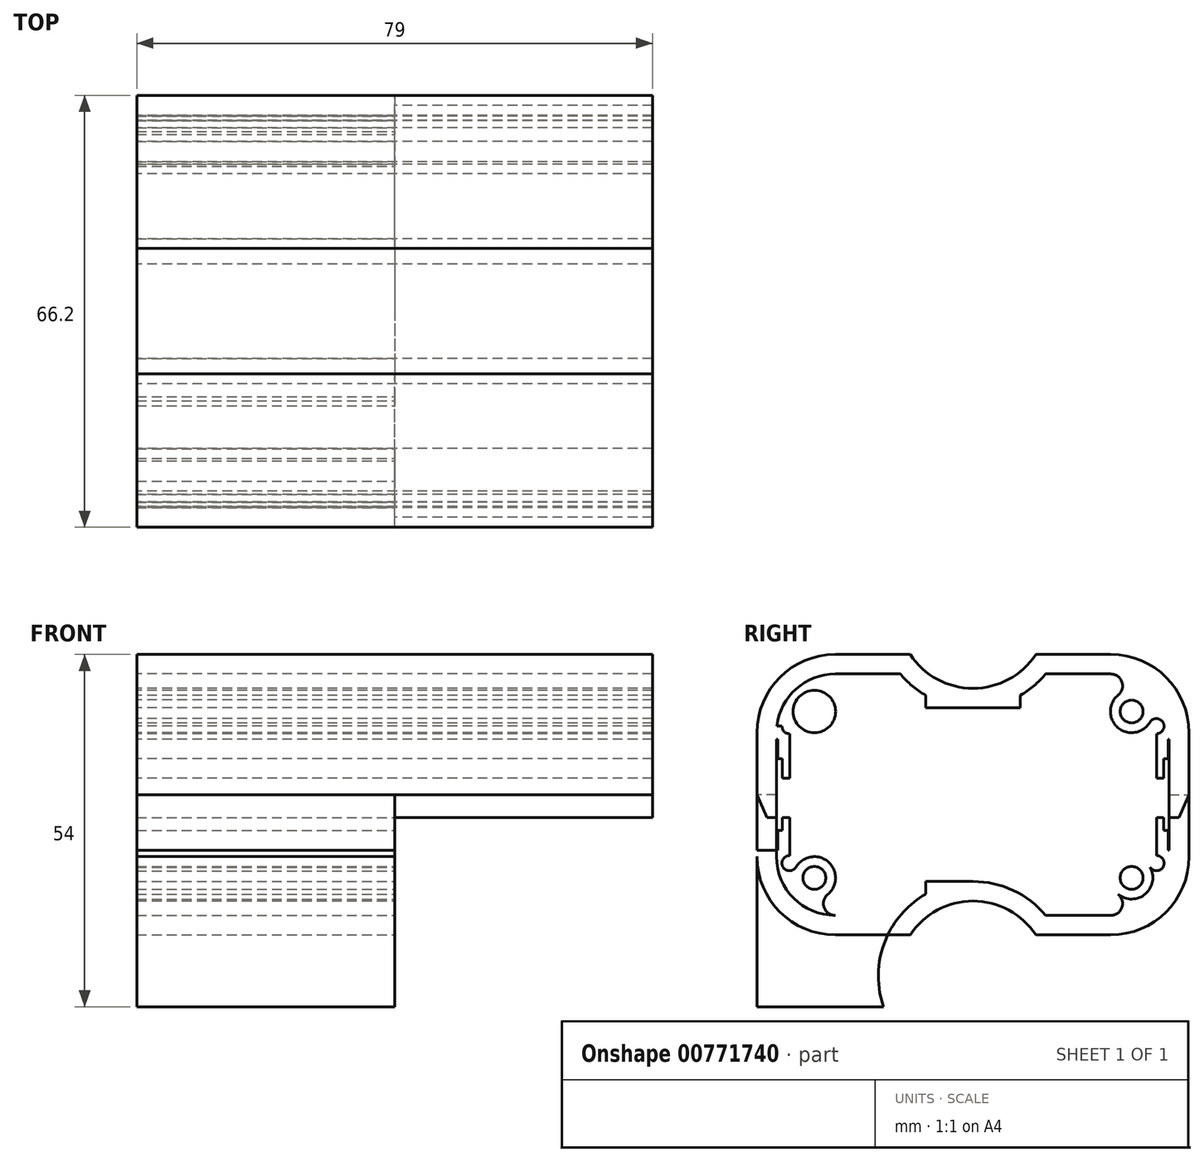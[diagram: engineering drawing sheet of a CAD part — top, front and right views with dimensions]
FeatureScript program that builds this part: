
annotation { "Feature Type Name" : "Feature", "Feature Type Description" : "" }
export const myFeature = defineFeature(function(context is Context, id is Id, definition is map)
    precondition{}
    {
        {
            var Q0;
            Q0=qCreatedBy(makeId("Right.planeOp"),FACE);
            var sketch = newSketch(context, id + "F0", { "sketchPlane" : qUnion([Q0])});
            skLineSegment(sketch, "E0.bottom", {"start": v(-33.1, -16.8) * mm, "end": v(-33.1, -3.8) * mm});
            skLineSegment(sketch, "E0.top", {"start": v(33.1, -16.8) * mm, "end": v(33.1, 19.2) * mm});
            skLineSegment(sketch, "E0.left", {"start": v(-33.1, -16.8) * mm, "end": v(33.1, -16.8) * mm});
            skLineSegment(sketch, "E0.right", {"start": v(-33.1, 19.2) * mm, "end": v(33.1, 19.2) * mm});
            skPoint(sketch, "E0.middle", {"position": v(0, 1.2) * mm});
            skLineSegment(sketch, "E1.bottom", {"start": v(-33.1, -16.8) * mm, "end": v(-33.1, 19.2) * mm});
            skLineSegment(sketch, "E1.right", {"start": v(-21.1, 8.2) * mm, "end": v(21.1, 8.2) * mm});
            skPoint(sketch, "E2.visualSharp", {"position": v(33.1, 8.2) * mm});
            skArc(sketch, "E2.filletArc", {"start": v(33.1, -3.8) * mm, "mid": v(29.59, 4.69) * mm, "end": v(21.1, 8.2) * mm});
            skPoint(sketch, "E3.newPointB", {"position": v(-33.1, 19.2) * mm});
            skArc(sketch, "E3.filletArc", {"start": v(-21.1, 8.2) * mm, "mid": v(-29.59, 4.69) * mm, "end": v(-33.1, -3.8) * mm});
            skLineSegment(sketch, "E4.0", {"start": v(-30.1, -16.8) * mm, "end": v(-30.1, -3.8) * mm});
            skLineSegment(sketch, "E4.1", {"start": v(30.04, -16.8) * mm, "end": v(30.04, -2.8) * mm});
            skArc(sketch, "E4.2", {"start": v(30.04, -2.8) * mm, "mid": v(27.1, 2.9) * mm, "end": v(21.1, 5.2) * mm});
            skLineSegment(sketch, "E4.3", {"start": v(-21.1, 5.2) * mm, "end": v(21.1, 5.2) * mm});
            skArc(sketch, "E4.4", {"start": v(-21.1, 5.2) * mm, "mid": v(-27.46, 2.56) * mm, "end": v(-30.1, -3.8) * mm});
            skCircle(sketch, "E5", {"center": v(0, 14.5) * mm, "radius": 11.5 * mm});
            skCircle(sketch, "E6.0", {"center": v(0, 14.5) * mm, "radius": 14.5 * mm});
            skLineSegment(sketch, "E7", {"start": v(0, 3) * mm, "end": v(0, 0) * mm, "construction": true});
            skLineSegment(sketch, "E8.left", {"start": v(7.25, 0) * mm, "end": v(-7.25, 0) * mm});
            skPoint(sketch, "E8.middle", {"position": v(0, 1.5) * mm});
            skCircle(sketch, "E9", {"center": v(24.3, -0.55) * mm, "radius": 1.75 * mm});
            skCircle(sketch, "E10.0", {"center": v(24.3, -0.55) * mm, "radius": 3.25 * mm});
            skLineSegment(sketch, "E11.top", {"start": v(28.1, -10.8) * mm, "end": v(28.1, -2.8) * mm});
            skLineSegment(sketch, "E11.right", {"start": v(33.1, -2.8) * mm, "end": v(28.1, -2.8) * mm});
            skLineSegment(sketch, "E12.bottom", {"start": v(28.1, -2.8) * mm, "end": v(28.1, -10.8) * mm});
            skLineSegment(sketch, "E13.left", {"start": v(28.1, -2.8) * mm, "end": v(30.04, -2.8) * mm});
            skLineSegment(sketch, "E13.right", {"start": v(29.9, -4.8) * mm, "end": v(33.1, -4.8) * mm});
            skLineSegment(sketch, "E14.top", {"start": v(29.9, -4.8) * mm, "end": v(29.9, -7.8) * mm});
            skLineSegment(sketch, "E14.left", {"start": v(30.04, -2.8) * mm, "end": v(33.1, -2.8) * mm});
            skLineSegment(sketch, "E14.right", {"start": v(29.2, -7.8) * mm, "end": v(29.9, -7.8) * mm});
            skLineSegment(sketch, "E15.top", {"start": v(29.2, -7.8) * mm, "end": v(29.2, -10.8) * mm});
            skLineSegment(sketch, "E15.right", {"start": v(28.1, -10.8) * mm, "end": v(29.2, -10.8) * mm});
            skCircle(sketch, "E16", {"center": v(21.1, 3.38) * mm, "radius": 1.82 * mm});
            skPoint(sketch, "E16.second.point", {"position": v(21.1, 5.2) * mm});
            skPoint(sketch, "E16.third.point", {"position": v(21.1, 5.2) * mm});
            skCircle(sketch, "E17", {"center": v(28.1, -2.8) * mm, "radius": 1.17 * mm});
            skLineSegment(sketch, "E18", {"start": v(28.1, -2.8) * mm, "end": v(28.92, -3.62) * mm, "construction": true});
            skLineSegment(sketch, "E19.bottom", {"start": v(33.1, -2.8) * mm, "end": v(33.1, -9.6) * mm});
            skLineSegment(sketch, "E19.top", {"start": v(30.04, -2.8) * mm, "end": v(30.04, -9.6) * mm});
            skLineSegment(sketch, "E19.left", {"start": v(33.1, -2.8) * mm, "end": v(30.04, -2.8) * mm});
            skLineSegment(sketch, "E19.right", {"start": v(33.1, -9.6) * mm, "end": v(30.04, -9.6) * mm});
            skLineSegment(sketch, "E20", {"start": v(33.1, -13.3) * mm, "end": v(31.57, -16.8) * mm});
            skLineSegment(sketch, "E21", {"start": v(33.1, -16.8) * mm, "end": v(30.04, -16.8) * mm, "construction": true});
            skLineSegment(sketch, "E22", {"start": v(0, -16.8) * mm, "end": v(0, 29) * mm, "construction": true});
            skCircle(sketch, "E23.MirrorC", {"center": v(-21.1, 3.38) * mm, "radius": 1.82 * mm});
            skCircle(sketch, "E24.MirrorC", {"center": v(-24.3, -0.55) * mm, "radius": 3.25 * mm});
            skCircle(sketch, "E25.MirrorC", {"center": v(-24.3, -0.55) * mm, "radius": 1.75 * mm});
            skCircle(sketch, "E26.MirrorC", {"center": v(-28.1, -2.8) * mm, "radius": 1.17 * mm});
            skLineSegment(sketch, "E27.MirrorCS", {"start": v(-28.1, -2.8) * mm, "end": v(-30.04, -2.8) * mm});
            skLineSegment(sketch, "E28.MirrorCS", {"start": v(-28.1, -2.8) * mm, "end": v(-28.1, -10.8) * mm});
            skLineSegment(sketch, "E29.MirrorCS", {"start": v(-28.1, -10.8) * mm, "end": v(-29.2, -10.8) * mm});
            skLineSegment(sketch, "E30.MirrorCS", {"start": v(-29.2, -7.8) * mm, "end": v(-29.2, -10.8) * mm});
            skLineSegment(sketch, "E31.MirrorCS", {"start": v(-29.2, -7.8) * mm, "end": v(-29.9, -7.8) * mm});
            skLineSegment(sketch, "E32.MirrorCS", {"start": v(-29.9, -4.8) * mm, "end": v(-29.9, -7.8) * mm});
            skLineSegment(sketch, "E33.MirrorCS", {"start": v(-29.9, -4.8) * mm, "end": v(-33.1, -4.8) * mm});
            skLineSegment(sketch, "E34.MirrorCS", {"start": v(-33.1, -13.3) * mm, "end": v(-31.57, -16.8) * mm});
            skLineSegment(sketch, "E35.bottom", {"start": v(33.1, -16.8) * mm, "end": v(33.1, 5.2) * mm, "construction": true});
            skLineSegment(sketch, "E35.top", {"start": v(21.1, -16.8) * mm, "end": v(21.1, 5.2) * mm, "construction": true});
            skLineSegment(sketch, "E35.left", {"start": v(33.1, -16.8) * mm, "end": v(21.1, -16.8) * mm, "construction": true});
            skLineSegment(sketch, "E35.right", {"start": v(33.1, 5.2) * mm, "end": v(21.1, 5.2) * mm, "construction": true});
            skLineSegment(sketch, "E36", {"start": v(7.25, 0) * mm, "end": v(7.25, 1.94) * mm});
            skLineSegment(sketch, "E37", {"start": v(7.25, 1.94) * mm, "end": v(-7.25, 1.94) * mm});
            skLineSegment(sketch, "E38", {"start": v(-7.25, 1.94) * mm, "end": v(-7.25, 0) * mm});
            skLineSegment(sketch, "E39", {"start": v(21.1, 5.2) * mm, "end": v(24.3, -0.55) * mm, "construction": true});
            skLineSegment(sketch, "E40", {"start": v(33.1, -13.3) * mm, "end": v(30.04, -13.3) * mm});
            skLineSegment(sketch, "E41", {"start": v(-33.1, -13.3) * mm, "end": v(-30.1, -13.3) * mm});
            skLineSegment(sketch, "E42", {"start": v(-53, -13.3) * mm, "end": v(50.01, -13.3) * mm, "construction": true});
            skLineSegment(sketch, "E43.MirrorCS", {"start": v(28.1, -23.8) * mm, "end": v(30.04, -23.8) * mm});
            skLineSegment(sketch, "E44.MirrorCS", {"start": v(28.1, -23.8) * mm, "end": v(28.92, -22.98) * mm, "construction": true});
            skCircle(sketch, "E45.MirrorC", {"center": v(28.1, -23.8) * mm, "radius": 1.17 * mm});
            skLineSegment(sketch, "E46.MirrorCS", {"start": v(33.1, -23.8) * mm, "end": v(30.04, -23.8) * mm});
            skLineSegment(sketch, "E47.MirrorCS", {"start": v(30.04, -23.8) * mm, "end": v(33.1, -23.8) * mm});
            skLineSegment(sketch, "E48.MirrorCS", {"start": v(28.1, -15.8) * mm, "end": v(29.2, -15.8) * mm});
            skLineSegment(sketch, "E49.MirrorCS", {"start": v(33.1, -23.8) * mm, "end": v(28.1, -23.8) * mm});
            skLineSegment(sketch, "E50.MirrorCS", {"start": v(28.1, -23.8) * mm, "end": v(28.1, -15.8) * mm});
            skCircle(sketch, "E51.MirrorC", {"center": v(-28.1, -23.8) * mm, "radius": 1.17 * mm});
            skLineSegment(sketch, "E52.MirrorCS", {"start": v(29.9, -21.8) * mm, "end": v(29.9, -18.8) * mm});
            skLineSegment(sketch, "E53.MirrorCS", {"start": v(29.2, -18.8) * mm, "end": v(29.2, -15.8) * mm});
            skLineSegment(sketch, "E54.MirrorCS", {"start": v(33.1, -17) * mm, "end": v(30.04, -17) * mm});
            skLineSegment(sketch, "E55.MirrorCS", {"start": v(30.04, -23.8) * mm, "end": v(30.04, -17) * mm});
            skLineSegment(sketch, "E56.MirrorCS", {"start": v(-28.1, -23.8) * mm, "end": v(-30.04, -23.8) * mm});
            skLineSegment(sketch, "E57.MirrorCS", {"start": v(33.1, -13.3) * mm, "end": v(31.57, -9.8) * mm});
            skLineSegment(sketch, "E58.MirrorCS", {"start": v(29.2, -18.8) * mm, "end": v(29.9, -18.8) * mm});
            skLineSegment(sketch, "E59.MirrorCS", {"start": v(7.25, -26.6) * mm, "end": v(7.25, -28.54) * mm});
            skLineSegment(sketch, "E60.MirrorCS", {"start": v(-29.2, -18.8) * mm, "end": v(-29.9, -18.8) * mm});
            skLineSegment(sketch, "E61.MirrorCS", {"start": v(-7.25, -28.54) * mm, "end": v(-7.25, -26.6) * mm});
            skLineSegment(sketch, "E62.MirrorCS", {"start": v(30.04, -9.8) * mm, "end": v(30.04, -23.8) * mm});
            skCircle(sketch, "E63.MirrorC", {"center": v(-24.3, -26.05) * mm, "radius": 1.75 * mm});
            skLineSegment(sketch, "E64.MirrorCS", {"start": v(29.9, -21.8) * mm, "end": v(33.1, -21.8) * mm});
            skLineSegment(sketch, "E65.MirrorCS", {"start": v(28.1, -15.8) * mm, "end": v(28.1, -23.8) * mm});
            skLineSegment(sketch, "E66.MirrorCS", {"start": v(-28.1, -15.8) * mm, "end": v(-29.2, -15.8) * mm});
            skLineSegment(sketch, "E67.MirrorCS", {"start": v(-29.9, -21.8) * mm, "end": v(-33.1, -21.8) * mm});
            skLineSegment(sketch, "E68.MirrorCS", {"start": v(-33.1, -13.3) * mm, "end": v(-31.57, -9.8) * mm});
            skLineSegment(sketch, "E69.MirrorCS", {"start": v(-29.9, -21.8) * mm, "end": v(-29.9, -18.8) * mm});
            skLineSegment(sketch, "E70.MirrorCS", {"start": v(-29.2, -18.8) * mm, "end": v(-29.2, -15.8) * mm});
            skLineSegment(sketch, "E71.MirrorCS", {"start": v(33.1, -9.8) * mm, "end": v(30.04, -9.8) * mm, "construction": true});
            skLineSegment(sketch, "E72.MirrorCS", {"start": v(33.1, -23.8) * mm, "end": v(33.1, -17) * mm});
            skLineSegment(sketch, "E73.MirrorCS", {"start": v(-30.1, -9.8) * mm, "end": v(-30.1, -22.8) * mm});
            skLineSegment(sketch, "E74.MirrorCS", {"start": v(-33.1, -9.8) * mm, "end": v(-33.1, -22.8) * mm});
            skLineSegment(sketch, "E75.MirrorCS", {"start": v(0, -29.6) * mm, "end": v(0, -26.6) * mm, "construction": true});
            skPoint(sketch, "E76.MirrorP", {"position": v(21.1, -31.8) * mm});
            skCircle(sketch, "E77.MirrorC", {"center": v(21.1, -29.98) * mm, "radius": 1.82 * mm});
            skCircle(sketch, "E78.MirrorC", {"center": v(-21.1, -29.98) * mm, "radius": 1.82 * mm});
            skLineSegment(sketch, "E79.MirrorCS", {"start": v(-28.1, -23.8) * mm, "end": v(-28.1, -15.8) * mm});
            skPoint(sketch, "E80.MirrorP", {"position": v(0, -28.1) * mm});
            skLineSegment(sketch, "E81.MirrorCS", {"start": v(33.1, -31.8) * mm, "end": v(21.1, -31.8) * mm, "construction": true});
            skLineSegment(sketch, "E82.MirrorCS", {"start": v(7.25, -28.54) * mm, "end": v(-7.25, -28.54) * mm});
            skPoint(sketch, "E83.MirrorP", {"position": v(33.1, -34.8) * mm});
            skLineSegment(sketch, "E84.MirrorCS", {"start": v(-33.1, -9.8) * mm, "end": v(33.1, -9.8) * mm});
            skArc(sketch, "E85.MirrorCS", {"start": v(-21.1, -34.8) * mm, "mid": v(-29.59, -31.29) * mm, "end": v(-33.1, -22.8) * mm});
            skLineSegment(sketch, "E86.MirrorCS", {"start": v(-21.1, -31.8) * mm, "end": v(21.1, -31.8) * mm});
            skArc(sketch, "E87.MirrorCS", {"start": v(30.04, -23.8) * mm, "mid": v(27.1, -29.5) * mm, "end": v(21.1, -31.8) * mm});
            skLineSegment(sketch, "E88.MirrorCS", {"start": v(-21.1, -34.8) * mm, "end": v(21.1, -34.8) * mm});
            skCircle(sketch, "E89.MirrorC", {"center": v(0, -41.1) * mm, "radius": 11.5 * mm});
            skLineSegment(sketch, "E90.MirrorCS", {"start": v(7.25, -26.6) * mm, "end": v(-7.25, -26.6) * mm});
            skCircle(sketch, "E91.MirrorC", {"center": v(24.3, -26.05) * mm, "radius": 1.75 * mm});
            skArc(sketch, "E92.MirrorCS", {"start": v(-21.1, -31.8) * mm, "mid": v(-27.46, -29.16) * mm, "end": v(-30.1, -22.8) * mm});
            skLineSegment(sketch, "E93.MirrorCS", {"start": v(0, -9.8) * mm, "end": v(0, -55.6) * mm, "construction": true});
            skPoint(sketch, "E94.MirrorP", {"position": v(0, -27.8) * mm});
            skCircle(sketch, "E95.MirrorC", {"center": v(-24.3, -26.05) * mm, "radius": 3.25 * mm});
            skCircle(sketch, "E96.MirrorC", {"center": v(24.3, -26.05) * mm, "radius": 3.25 * mm});
            skLineSegment(sketch, "E97.MirrorCS", {"start": v(-33.1, -45.8) * mm, "end": v(33.1, -45.8) * mm});
            skLineSegment(sketch, "E98.MirrorCS", {"start": v(33.1, -9.8) * mm, "end": v(21.1, -9.8) * mm, "construction": true});
            skLineSegment(sketch, "E99.MirrorCS", {"start": v(21.1, -9.8) * mm, "end": v(21.1, -31.8) * mm, "construction": true});
            skLineSegment(sketch, "E100.MirrorCS", {"start": v(-33.1, -9.8) * mm, "end": v(-33.1, -45.8) * mm});
            skCircle(sketch, "E101.MirrorC", {"center": v(0, -41.1) * mm, "radius": 14.5 * mm});
            skPoint(sketch, "E102.MirrorP", {"position": v(-33.1, -45.8) * mm});
            skLineSegment(sketch, "E103.MirrorCS", {"start": v(33.1, -9.8) * mm, "end": v(33.1, -45.8) * mm});
            skLineSegment(sketch, "E104.MirrorCS", {"start": v(33.1, -9.8) * mm, "end": v(33.1, -31.8) * mm, "construction": true});
            skLineSegment(sketch, "E105.MirrorCS", {"start": v(21.1, -31.8) * mm, "end": v(24.3, -26.05) * mm, "construction": true});
            skArc(sketch, "E106.MirrorCS", {"start": v(33.1, -22.8) * mm, "mid": v(29.59, -31.29) * mm, "end": v(21.1, -34.8) * mm});
            skSolve(sketch);
        }
        {
            var Q0;
            {var subQ0=sQuery(id+"F0.wireOp",EDGE,"E6.0");var subQ1=sQuery(id+"F0.wireOp",EDGE,"E1.right");var subQ2=makeQuery(id+"F0.imprint","INTERSECT",VERTEX,{"disambiguationData":[OD(0.0)],"derivedFrom":[subQ1,subQ0]});Q0=makeQuery(id+"F0.imprint","IMPRINT",FACE,{"disambiguationData":[TD([[makeQuery(id+"F0.imprint","IMPRINT",EDGE,{"disambiguationData":[TD([[subQ2,-1.0]])],"derivedFrom":subQ1}),-1.0]])]});}
            var Q1;
            {var subQ0=sQuery(id+"F0.wireOp",EDGE,"E37");Q1=makeQuery(id+"F0.imprint","IMPRINT",FACE,{"disambiguationData":[TD([[makeQuery(id+"F0.imprint","IMPRINT",EDGE,{"derivedFrom":subQ0}),-1.0]])]});}
            var Q2;
            {var subQ0=sQuery(id+"F0.wireOp",EDGE,"E38");Q2=makeQuery(id+"F0.imprint","IMPRINT",FACE,{"disambiguationData":[TD([[makeQuery(id+"F0.imprint","IMPRINT",EDGE,{"derivedFrom":subQ0}),1.0]])]});}
            var Q3;
            {var subQ0=sQuery(id+"F0.wireOp",EDGE,"E37");Q3=makeQuery(id+"F0.imprint","IMPRINT",FACE,{"disambiguationData":[TD([[makeQuery(id+"F0.imprint","IMPRINT",EDGE,{"derivedFrom":subQ0}),1.0]])]});}
            var Q4;
            {var subQ0=sQuery(id+"F0.wireOp",EDGE,"E36");Q4=makeQuery(id+"F0.imprint","IMPRINT",FACE,{"disambiguationData":[TD([[makeQuery(id+"F0.imprint","IMPRINT",EDGE,{"derivedFrom":subQ0}),1.0]])]});}
            var Q5;
            {var subQ0=sQuery(id+"F0.wireOp",EDGE,"E5");var subQ1=sQuery(id+"F0.wireOp",EDGE,"E1.right");var subQ2=makeQuery(id+"F0.imprint","INTERSECT",VERTEX,{"disambiguationData":[OD(1.0)],"derivedFrom":[subQ1,subQ0]});Q5=makeQuery(id+"F0.imprint","IMPRINT",FACE,{"disambiguationData":[TD([[makeQuery(id+"F0.imprint","IMPRINT",EDGE,{"disambiguationData":[TD([[subQ2,-1.0]])],"derivedFrom":subQ1}),-1.0]])]});}
            var Q6;
            {var subQ1=sQuery(id+"F0.wireOp",EDGE,"E4.2");Q6=makeQuery(id+"F0.imprint","IMPRINT",FACE,{"disambiguationData":[TD([[makeQuery(id+"F0.imprint","IMPRINT",EDGE,{"derivedFrom":subQ1}),-1.0]])]});}
            var Q7;
            {var subQ1=sQuery(id+"F0.wireOp",EDGE,"E4.2");Q7=makeQuery(id+"F0.imprint","IMPRINT",FACE,{"disambiguationData":[TD([[makeQuery(id+"F0.imprint","IMPRINT",EDGE,{"derivedFrom":subQ1}),1.0]])]});}
            var Q8;
            Q8=makeQuery(id+"F0.imprint","IMPRINT",FACE,{"disambiguationData":[TD([[makeQuery(id+"F0.imprint","IMPRINT",EDGE,{"derivedFrom":sQuery(id+"F0.wireOp",EDGE,"E9")}),-1.0]])]});
            var Q9;
            {var subQ0=sQuery(id+"F0.wireOp",EDGE,"E14.top");Q9=makeQuery(id+"F0.imprint","IMPRINT",FACE,{"disambiguationData":[TD([[makeQuery(id+"F0.imprint","IMPRINT",EDGE,{"derivedFrom":subQ0}),-1.0]])]});}
            var Q10;
            {var subQ5=sQuery(id+"F0.wireOp",EDGE,"E19.bottom");var subQ6=sQuery(id+"F0.wireOp",EDGE,"E2.filletArc");var subQ7=makeQuery(id+"F0.imprint","INTERSECT",VERTEX,{"derivedFrom":[subQ6,subQ5]});Q10=makeQuery(id+"F0.imprint","IMPRINT",FACE,{"disambiguationData":[TD([[makeQuery(id+"F0.imprint","IMPRINT",EDGE,{"disambiguationData":[TD([[subQ7,-1.0]])],"derivedFrom":subQ6}),1.0]])]});}
            var Q11;
            {var subQ5=sQuery(id+"F0.wireOp",EDGE,"E19.right");Q11=makeQuery(id+"F0.imprint","IMPRINT",FACE,{"disambiguationData":[TD([[makeQuery(id+"F0.imprint","IMPRINT",EDGE,{"derivedFrom":subQ5}),-1.0]])]});}
            var Q12;
            {var subQ0=sQuery(id+"F0.wireOp",EDGE,"E19.right");Q12=makeQuery(id+"F0.imprint","IMPRINT",FACE,{"disambiguationData":[TD([[makeQuery(id+"F0.imprint","IMPRINT",EDGE,{"derivedFrom":subQ0}),1.0]])]});}
            var Q13;
            {var subQ0=sQuery(id+"F0.wireOp",EDGE,"E3.filletArc");Q13=makeQuery(id+"F0.imprint","IMPRINT",FACE,{"disambiguationData":[TD([[makeQuery(id+"F0.imprint","IMPRINT",EDGE,{"derivedFrom":subQ0}),1.0]])]});}
            var Q14;
            {var subQ1=sQuery(id+"F0.wireOp",EDGE,"E24.MirrorC");var subQ5=sQuery(id+"F0.wireOp",EDGE,"E23.MirrorC");var subQ6=makeQuery(id+"F0.imprint","INTERSECT",VERTEX,{"derivedFrom":[subQ5,subQ1]});Q14=makeQuery(id+"F0.imprint","IMPRINT",FACE,{"disambiguationData":[TD([[makeQuery(id+"F0.imprint","IMPRINT",EDGE,{"disambiguationData":[TD([[subQ6,1.0]])],"derivedFrom":subQ1}),1.0]])]});}
            var Q15;
            Q15=makeQuery(id+"F0.imprint","IMPRINT",FACE,{"disambiguationData":[TD([[makeQuery(id+"F0.imprint","IMPRINT",EDGE,{"derivedFrom":sQuery(id+"F0.wireOp",EDGE,"E25.MirrorC")}),1.0]])]});
            var Q16;
            {var subQ12=sQuery(id+"F0.wireOp",EDGE,"E29.MirrorCS");Q16=makeQuery(id+"F0.imprint","IMPRINT",FACE,{"disambiguationData":[TD([[makeQuery(id+"F0.imprint","IMPRINT",EDGE,{"derivedFrom":subQ12}),-1.0]])]});}
            var Q17;
            {var subQ3=sQuery(id+"F0.wireOp",EDGE,"E41");Q17=makeQuery(id+"F0.imprint","IMPRINT",FACE,{"disambiguationData":[TD([[makeQuery(id+"F0.imprint","IMPRINT",EDGE,{"derivedFrom":subQ3}),1.0]])]});}
            var Q18;
            {var subQ5=sQuery(id+"F0.wireOp",EDGE,"E31.MirrorCS");Q18=makeQuery(id+"F0.imprint","IMPRINT",FACE,{"disambiguationData":[TD([[makeQuery(id+"F0.imprint","IMPRINT",EDGE,{"derivedFrom":subQ5}),-1.0]])]});}
            var Q19;
            {var subQ0=sQuery(id+"F0.wireOp",EDGE,"E33.MirrorCS");var subQ1=sQuery(id+"F0.wireOp",EDGE,"E1.bottom");var subQ2=makeQuery(id+"F0.imprint","INTERSECT",VERTEX,{"derivedFrom":[subQ1,subQ0]});Q19=makeQuery(id+"F0.imprint","IMPRINT",FACE,{"disambiguationData":[TD([[makeQuery(id+"F0.imprint","IMPRINT",EDGE,{"disambiguationData":[TD([[subQ2,1.0]])],"derivedFrom":subQ0}),1.0]])]});}
            var Q20;
            {var subQ0=sQuery(id+"F0.wireOp",EDGE,"E68.MirrorCS");Q20=makeQuery(id+"F0.imprint","IMPRINT",FACE,{"disambiguationData":[TD([[makeQuery(id+"F0.imprint","IMPRINT",EDGE,{"derivedFrom":subQ0}),-1.0]])]});}
            var Q21;
            {var subQ0=sQuery(id+"F0.wireOp",EDGE,"E68.MirrorCS");Q21=makeQuery(id+"F0.imprint","IMPRINT",FACE,{"disambiguationData":[TD([[makeQuery(id+"F0.imprint","IMPRINT",EDGE,{"derivedFrom":subQ0}),1.0]])]});}
            var Q22;
            {var subQ0=sQuery(id+"F0.wireOp",EDGE,"E57.MirrorCS");Q22=makeQuery(id+"F0.imprint","IMPRINT",FACE,{"disambiguationData":[TD([[makeQuery(id+"F0.imprint","IMPRINT",EDGE,{"derivedFrom":subQ0}),1.0]])]});}
            var Q23;
            {var subQ0=sQuery(id+"F0.wireOp",EDGE,"E57.MirrorCS");Q23=makeQuery(id+"F0.imprint","IMPRINT",FACE,{"disambiguationData":[TD([[makeQuery(id+"F0.imprint","IMPRINT",EDGE,{"derivedFrom":subQ0}),-1.0]])]});}
            var Q24;
            {var subQ0=sQuery(id+"F0.wireOp",EDGE,"E15.right");Q24=makeQuery(id+"F0.imprint","IMPRINT",FACE,{"disambiguationData":[TD([[makeQuery(id+"F0.imprint","IMPRINT",EDGE,{"derivedFrom":subQ0}),1.0]])]});}
            extrude(context, id + "F1", {"entities" : qUnion([Q0, Q1, Q2, Q3, Q4, Q5, Q6, Q7, Q8, Q9, Q10, Q11, Q12, Q13, Q14, Q15, Q16, Q17, Q18, Q19, Q20, Q21, Q22, Q23, Q24]), "depth" : 79 * mm, "offsetDistance" : 25 * mm, "symmetric" : true});
        }
        {
            var Q0;
            {var subQ0=sQuery(id+"F0.wireOp",EDGE,"E34.MirrorCS");Q0=makeQuery(id+"F0.imprint","IMPRINT",FACE,{"disambiguationData":[TD([[makeQuery(id+"F0.imprint","IMPRINT",EDGE,{"derivedFrom":subQ0}),1.0]])]});}
            var Q1;
            {var subQ0=sQuery(id+"F0.wireOp",EDGE,"E20");Q1=makeQuery(id+"F0.imprint","IMPRINT",FACE,{"disambiguationData":[TD([[makeQuery(id+"F0.imprint","IMPRINT",EDGE,{"derivedFrom":subQ0}),-1.0]])]});}
            var Q2;
            Q2=makeQuery(id+"F1.opExtrude","CAP_FACE",FACE,{"disambiguationData":[OSD([sQuery(id+"F0.wireOp",EDGE,"E0.top"),sQuery(id+"F0.wireOp",EDGE,"E1.bottom"),sQuery(id+"F0.wireOp",EDGE,"E1.right"),sQuery(id+"F0.wireOp",EDGE,"E2.filletArc"),sQuery(id+"F0.wireOp",EDGE,"E3.filletArc"),sQuery(id+"F0.wireOp",EDGE,"E4.0"),sQuery(id+"F0.wireOp",EDGE,"E4.1"),sQuery(id+"F0.wireOp",EDGE,"E4.3"),sQuery(id+"F0.wireOp",EDGE,"E5"),sQuery(id+"F0.wireOp",EDGE,"E6.0"),sQuery(id+"F0.wireOp",EDGE,"E8.left"),sQuery(id+"F0.wireOp",EDGE,"E9"),sQuery(id+"F0.wireOp",EDGE,"E10.0"),sQuery(id+"F0.wireOp",EDGE,"E13.right"),sQuery(id+"F0.wireOp",EDGE,"E14.top"),sQuery(id+"F0.wireOp",EDGE,"E14.right"),sQuery(id+"F0.wireOp",EDGE,"E12.bottom"),sQuery(id+"F0.wireOp",EDGE,"E15.top"),sQuery(id+"F0.wireOp",EDGE,"E15.right"),sQuery(id+"F0.wireOp",EDGE,"E16"),sQuery(id+"F0.wireOp",EDGE,"E17"),sQuery(id+"F0.wireOp",EDGE,"E19.bottom"),sQuery(id+"F0.wireOp",EDGE,"E19.top"),sQuery(id+"F0.wireOp",EDGE,"E23.MirrorC"),sQuery(id+"F0.wireOp",EDGE,"E24.MirrorC"),sQuery(id+"F0.wireOp",EDGE,"E25.MirrorC"),sQuery(id+"F0.wireOp",EDGE,"E26.MirrorC"),sQuery(id+"F0.wireOp",EDGE,"E28.MirrorCS"),sQuery(id+"F0.wireOp",EDGE,"E29.MirrorCS"),sQuery(id+"F0.wireOp",EDGE,"E30.MirrorCS"),sQuery(id+"F0.wireOp",EDGE,"E31.MirrorCS"),sQuery(id+"F0.wireOp",EDGE,"E32.MirrorCS"),sQuery(id+"F0.wireOp",EDGE,"E33.MirrorCS"),sQuery(id+"F0.wireOp",EDGE,"E36"),sQuery(id+"F0.wireOp",EDGE,"E38"),sQuery(id+"F0.wireOp",EDGE,"E62.MirrorCS"),sQuery(id+"F0.wireOp",EDGE,"E40"),sQuery(id+"F0.wireOp",EDGE,"E73.MirrorCS"),sQuery(id+"F0.wireOp",EDGE,"E41"),sQuery(id+"F0.wireOp",EDGE,"E100.MirrorCS"),sQuery(id+"F0.wireOp",EDGE,"E103.MirrorCS")])],"isStart":false});
            extrude(context, id + "F2", {"entities" : qUnion([Q0, Q1]), "operationType" : NewBodyOperationType.ADD, "endBound" : BoundingType.UP_TO_SURFACE, "depth" : 25 * mm, "endBoundEntityFace" : qUnion([Q2]), "offsetDistance" : 25 * mm});
        }
        {
            var Q0;
            {var subQ0=sQuery(id+"F0.wireOp",EDGE,"E34.MirrorCS");Q0=makeQuery(id+"F0.imprint","IMPRINT",FACE,{"disambiguationData":[TD([[makeQuery(id+"F0.imprint","IMPRINT",EDGE,{"derivedFrom":subQ0}),1.0]])]});}
            var Q1;
            {var subQ3=sQuery(id+"F0.wireOp",EDGE,"E34.MirrorCS");Q1=makeQuery(id+"F0.imprint","IMPRINT",FACE,{"disambiguationData":[TD([[makeQuery(id+"F0.imprint","IMPRINT",EDGE,{"derivedFrom":subQ3}),-1.0]])]});}
            var Q2;
            {var subQ1=sQuery(id+"F0.wireOp",EDGE,"E0.left");var subQ5=sQuery(id+"F0.wireOp",EDGE,"E100.MirrorCS");var subQ8=makeQuery(id+"F0.imprint","INTERSECT",VERTEX,{"derivedFrom":[subQ1,subQ5]});Q2=makeQuery(id+"F0.imprint","IMPRINT",FACE,{"disambiguationData":[TD([[makeQuery(id+"F0.imprint","IMPRINT",EDGE,{"disambiguationData":[TD([[subQ8,-1.0]])],"derivedFrom":subQ1}),-1.0]])]});}
            var Q3;
            {var subQ3=sQuery(id+"F0.wireOp",EDGE,"E20");Q3=makeQuery(id+"F0.imprint","IMPRINT",FACE,{"disambiguationData":[TD([[makeQuery(id+"F0.imprint","IMPRINT",EDGE,{"derivedFrom":subQ3}),1.0]])]});}
            var Q4;
            {var subQ0=sQuery(id+"F0.wireOp",EDGE,"E20");Q4=makeQuery(id+"F0.imprint","IMPRINT",FACE,{"disambiguationData":[TD([[makeQuery(id+"F0.imprint","IMPRINT",EDGE,{"derivedFrom":subQ0}),-1.0]])]});}
            var Q5;
            {var subQ0=sQuery(id+"F0.wireOp",EDGE,"E54.MirrorCS");Q5=makeQuery(id+"F0.imprint","IMPRINT",FACE,{"disambiguationData":[TD([[makeQuery(id+"F0.imprint","IMPRINT",EDGE,{"derivedFrom":subQ0}),1.0]])]});}
            var Q6;
            {var subQ0=sQuery(id+"F0.wireOp",EDGE,"E103.MirrorCS");var subQ1=sQuery(id+"F0.wireOp",EDGE,"E64.MirrorCS");var subQ2=makeQuery(id+"F0.imprint","INTERSECT",VERTEX,{"derivedFrom":[subQ1,subQ0]});Q6=makeQuery(id+"F0.imprint","IMPRINT",FACE,{"disambiguationData":[TD([[makeQuery(id+"F0.imprint","IMPRINT",EDGE,{"disambiguationData":[TD([[subQ2,1.0]])],"derivedFrom":subQ1}),-1.0]])]});}
            var Q7;
            {var subQ0=sQuery(id+"F0.wireOp",EDGE,"E52.MirrorCS");Q7=makeQuery(id+"F0.imprint","IMPRINT",FACE,{"disambiguationData":[TD([[makeQuery(id+"F0.imprint","IMPRINT",EDGE,{"derivedFrom":subQ0}),1.0]])]});}
            var Q8;
            {var subQ5=sQuery(id+"F0.wireOp",EDGE,"E87.MirrorCS");Q8=makeQuery(id+"F0.imprint","IMPRINT",FACE,{"disambiguationData":[TD([[makeQuery(id+"F0.imprint","IMPRINT",EDGE,{"derivedFrom":subQ5}),1.0]])]});}
            var Q9;
            {var subQ0=sQuery(id+"F0.wireOp",EDGE,"E87.MirrorCS");Q9=makeQuery(id+"F0.imprint","IMPRINT",FACE,{"disambiguationData":[TD([[makeQuery(id+"F0.imprint","IMPRINT",EDGE,{"derivedFrom":subQ0}),-1.0]])]});}
            var Q10;
            Q10=makeQuery(id+"F0.imprint","IMPRINT",FACE,{"disambiguationData":[TD([[makeQuery(id+"F0.imprint","IMPRINT",EDGE,{"derivedFrom":sQuery(id+"F0.wireOp",EDGE,"E91.MirrorC")}),1.0]])]});
            var Q11;
            {var subQ0=sQuery(id+"F0.wireOp",EDGE,"E89.MirrorC");var subQ1=sQuery(id+"F0.wireOp",EDGE,"E86.MirrorCS");var subQ2=makeQuery(id+"F0.imprint","INTERSECT",VERTEX,{"disambiguationData":[OD(1.0)],"derivedFrom":[subQ1,subQ0]});Q11=makeQuery(id+"F0.imprint","IMPRINT",FACE,{"disambiguationData":[TD([[makeQuery(id+"F0.imprint","IMPRINT",EDGE,{"disambiguationData":[TD([[subQ2,-1.0]])],"derivedFrom":subQ1}),-1.0]])]});}
            var Q12;
            {var subQ7=sQuery(id+"F0.wireOp",EDGE,"E82.MirrorCS");Q12=makeQuery(id+"F0.imprint","IMPRINT",FACE,{"disambiguationData":[TD([[makeQuery(id+"F0.imprint","IMPRINT",EDGE,{"derivedFrom":subQ7}),1.0]])]});}
            var Q13;
            {var subQ0=sQuery(id+"F0.wireOp",EDGE,"E82.MirrorCS");Q13=makeQuery(id+"F0.imprint","IMPRINT",FACE,{"disambiguationData":[TD([[makeQuery(id+"F0.imprint","IMPRINT",EDGE,{"derivedFrom":subQ0}),-1.0]])]});}
            var Q14;
            {var subQ0=sQuery(id+"F0.wireOp",EDGE,"E61.MirrorCS");Q14=makeQuery(id+"F0.imprint","IMPRINT",FACE,{"disambiguationData":[TD([[makeQuery(id+"F0.imprint","IMPRINT",EDGE,{"derivedFrom":subQ0}),-1.0]])]});}
            var Q15;
            {var subQ0=sQuery(id+"F0.wireOp",EDGE,"E101.MirrorC");var subQ1=sQuery(id+"F0.wireOp",EDGE,"E86.MirrorCS");var subQ2=makeQuery(id+"F0.imprint","INTERSECT",VERTEX,{"disambiguationData":[OD(0.0)],"derivedFrom":[subQ1,subQ0]});Q15=makeQuery(id+"F0.imprint","IMPRINT",FACE,{"disambiguationData":[TD([[makeQuery(id+"F0.imprint","IMPRINT",EDGE,{"disambiguationData":[TD([[subQ2,-1.0]])],"derivedFrom":subQ1}),-1.0]])]});}
            var Q16;
            {var subQ0=sQuery(id+"F0.wireOp",EDGE,"E85.MirrorCS");Q16=makeQuery(id+"F0.imprint","IMPRINT",FACE,{"disambiguationData":[TD([[makeQuery(id+"F0.imprint","IMPRINT",EDGE,{"derivedFrom":subQ0}),-1.0]])]});}
            var Q17;
            {var subQ5=sQuery(id+"F0.wireOp",EDGE,"E56.MirrorCS");var subQ7=sQuery(id+"F0.wireOp",EDGE,"E51.MirrorC");var subQ8=makeQuery(id+"F0.imprint","INTERSECT",VERTEX,{"derivedFrom":[subQ7,subQ5]});Q17=makeQuery(id+"F0.imprint","IMPRINT",FACE,{"disambiguationData":[TD([[makeQuery(id+"F0.imprint","IMPRINT",EDGE,{"disambiguationData":[TD([[subQ8,-1.0]])],"derivedFrom":subQ7}),-1.0]])]});}
            var Q18;
            Q18=makeQuery(id+"F0.imprint","IMPRINT",FACE,{"disambiguationData":[TD([[makeQuery(id+"F0.imprint","IMPRINT",EDGE,{"derivedFrom":sQuery(id+"F0.wireOp",EDGE,"E63.MirrorC")}),-1.0]])]});
            var Q19;
            {var subQ0=sQuery(id+"F0.wireOp",EDGE,"E60.MirrorCS");Q19=makeQuery(id+"F0.imprint","IMPRINT",FACE,{"disambiguationData":[TD([[makeQuery(id+"F0.imprint","IMPRINT",EDGE,{"derivedFrom":subQ0}),1.0]])]});}
            var Q20;
            {var subQ1=sQuery(id+"F0.wireOp",EDGE,"E54.MirrorCS");Q20=makeQuery(id+"F0.imprint","IMPRINT",FACE,{"disambiguationData":[TD([[makeQuery(id+"F0.imprint","IMPRINT",EDGE,{"derivedFrom":subQ1}),-1.0]])]});}
            var Q21;
            Q21=makeQuery(id+"F1.opExtrude","CAP_FACE",FACE,{"disambiguationData":[OSD([sQuery(id+"F0.wireOp",EDGE,"E0.top"),sQuery(id+"F0.wireOp",EDGE,"E1.bottom"),sQuery(id+"F0.wireOp",EDGE,"E1.right"),sQuery(id+"F0.wireOp",EDGE,"E2.filletArc"),sQuery(id+"F0.wireOp",EDGE,"E3.filletArc"),sQuery(id+"F0.wireOp",EDGE,"E4.0"),sQuery(id+"F0.wireOp",EDGE,"E4.1"),sQuery(id+"F0.wireOp",EDGE,"E4.3"),sQuery(id+"F0.wireOp",EDGE,"E5"),sQuery(id+"F0.wireOp",EDGE,"E6.0"),sQuery(id+"F0.wireOp",EDGE,"E8.left"),sQuery(id+"F0.wireOp",EDGE,"E9"),sQuery(id+"F0.wireOp",EDGE,"E10.0"),sQuery(id+"F0.wireOp",EDGE,"E13.right"),sQuery(id+"F0.wireOp",EDGE,"E14.top"),sQuery(id+"F0.wireOp",EDGE,"E14.right"),sQuery(id+"F0.wireOp",EDGE,"E12.bottom"),sQuery(id+"F0.wireOp",EDGE,"E15.top"),sQuery(id+"F0.wireOp",EDGE,"E15.right"),sQuery(id+"F0.wireOp",EDGE,"E16"),sQuery(id+"F0.wireOp",EDGE,"E17"),sQuery(id+"F0.wireOp",EDGE,"E19.bottom"),sQuery(id+"F0.wireOp",EDGE,"E19.top"),sQuery(id+"F0.wireOp",EDGE,"E23.MirrorC"),sQuery(id+"F0.wireOp",EDGE,"E24.MirrorC"),sQuery(id+"F0.wireOp",EDGE,"E25.MirrorC"),sQuery(id+"F0.wireOp",EDGE,"E26.MirrorC"),sQuery(id+"F0.wireOp",EDGE,"E28.MirrorCS"),sQuery(id+"F0.wireOp",EDGE,"E29.MirrorCS"),sQuery(id+"F0.wireOp",EDGE,"E30.MirrorCS"),sQuery(id+"F0.wireOp",EDGE,"E31.MirrorCS"),sQuery(id+"F0.wireOp",EDGE,"E32.MirrorCS"),sQuery(id+"F0.wireOp",EDGE,"E33.MirrorCS"),sQuery(id+"F0.wireOp",EDGE,"E36"),sQuery(id+"F0.wireOp",EDGE,"E38"),sQuery(id+"F0.wireOp",EDGE,"E62.MirrorCS"),sQuery(id+"F0.wireOp",EDGE,"E40"),sQuery(id+"F0.wireOp",EDGE,"E73.MirrorCS"),sQuery(id+"F0.wireOp",EDGE,"E41"),sQuery(id+"F0.wireOp",EDGE,"E100.MirrorCS"),sQuery(id+"F0.wireOp",EDGE,"E103.MirrorCS")])],"isStart":true});
            extrude(context, id + "F3", {"entities" : qUnion([Q0, Q1, Q2, Q3, Q4, Q5, Q6, Q7, Q8, Q9, Q10, Q11, Q12, Q13, Q14, Q15, Q16, Q17, Q18, Q19, Q20]), "endBound" : BoundingType.UP_TO_SURFACE, "oppositeDirection" : true, "depth" : 25 * mm, "endBoundEntityFace" : qUnion([Q21]), "offsetDistance" : 25 * mm});
        }
    });
